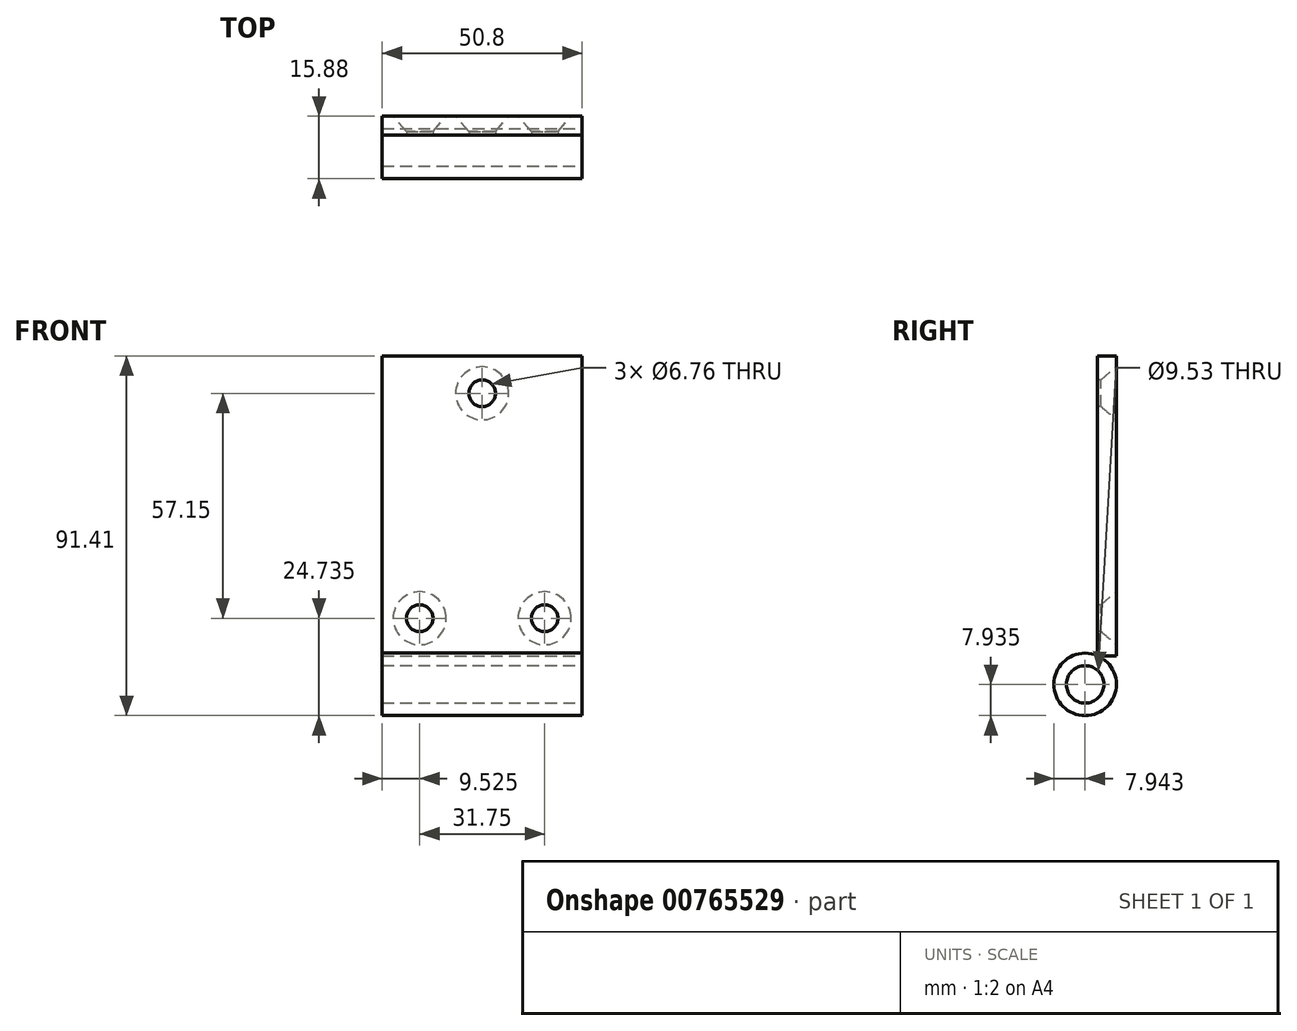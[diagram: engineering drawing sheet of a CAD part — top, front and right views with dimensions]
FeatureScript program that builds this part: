
annotation { "Feature Type Name" : "Feature", "Feature Type Description" : "" }
export const myFeature = defineFeature(function(context is Context, id is Id, definition is map)
    precondition{}
    {
        {
            var Q0;
            Q0=qCreatedBy(makeId("Front.planeOp"),FACE);
            var sketch = newSketch(context, id + "F0", { "sketchPlane" : qUnion([Q0])});
            skLineSegment(sketch, "E0.bottom", {"start": v(-25.4, 38.1) * mm, "end": v(25.4, 38.1) * mm});
            skLineSegment(sketch, "E0.top", {"start": v(-25.4, -38.1) * mm, "end": v(25.4, -38.1) * mm});
            skLineSegment(sketch, "E0.left", {"start": v(-25.4, 38.1) * mm, "end": v(-25.4, -38.1) * mm});
            skLineSegment(sketch, "E0.right", {"start": v(25.4, 38.1) * mm, "end": v(25.4, -38.1) * mm});
            skPoint(sketch, "E0.middle", {"position": v(0, 0) * mm});
            skCircle(sketch, "E1", {"center": v(0, 28.57) * mm, "radius": 3.43 * mm});
            skCircle(sketch, "E2", {"center": v(-15.87, -28.58) * mm, "radius": 3.43 * mm});
            skCircle(sketch, "E3", {"center": v(15.88, -28.58) * mm, "radius": 3.43 * mm});
            skSolve(sketch);
        }
        {
            var Q0;
            Q0=makeQuery(id+"F0.imprint","IMPRINT",FACE,{"disambiguationData":[TD([[makeQuery(id+"F0.imprint","IMPRINT",EDGE,{"derivedFrom":sQuery(id+"F0.wireOp",EDGE,"E0.bottom")}),-1.0]])]});
            var Q1;
            Q1=makeQuery(id+"F0.imprint","IMPRINT",FACE,{"disambiguationData":[TD([[makeQuery(id+"F0.imprint","IMPRINT",EDGE,{"derivedFrom":sQuery(id+"F0.wireOp",EDGE,"E1")}),1.0]])]});
            var Q2;
            Q2=makeQuery(id+"F0.imprint","IMPRINT",FACE,{"disambiguationData":[TD([[makeQuery(id+"F0.imprint","IMPRINT",EDGE,{"derivedFrom":sQuery(id+"F0.wireOp",EDGE,"E2")}),1.0]])]});
            var Q3;
            Q3=makeQuery(id+"F0.imprint","IMPRINT",FACE,{"disambiguationData":[TD([[makeQuery(id+"F0.imprint","IMPRINT",EDGE,{"derivedFrom":sQuery(id+"F0.wireOp",EDGE,"E3")}),1.0]])]});
            extrude(context, id + "F1", {"entities" : qUnion([Q0, Q1, Q2, Q3]), "depth" : 4.76 * mm, "offsetDistance" : 25.4 * mm});
        }
        {
            var Q0;
            Q0=sQuery(id+"F0.wireOp",VERTEX,"E1.center");
            var Q1;
            Q1=sQuery(id+"F0.wireOp",VERTEX,"E2.center");
            var Q2;
            Q2=sQuery(id+"F0.wireOp",VERTEX,"E3.center");
            var Q3;
            Q3=makeQuery(id+"F1.opExtrude","SWEPT_BODY",BODY,{"disambiguationData":[OSD([sQuery(id+"F0.wireOp",EDGE,"E0.bottom"),sQuery(id+"F0.wireOp",EDGE,"E0.top"),sQuery(id+"F0.wireOp",EDGE,"E0.left"),sQuery(id+"F0.wireOp",EDGE,"E0.right")])]});
            hole(context, id + "F2", {"style" : HoleStyle.C_SINK, "endStyle" : HoleEndStyle.THROUGH, "oppositeDirection" : true, "standardTappedOrClearance" : lookupTablePath({ "fit" : "Normal (ASME)", "standard" : "ANSI", "size" : "1/4", "type" : "Clearance" }), "standardBlindInLast" : lookupTablePath({ "fit" : "Free", "standard" : "ANSI", "size" : "1/4", "type" : "Clearance" }), "holeDiameter" : 6.76 * mm, "cSinkDiameter" : 13.5 * mm, "cSinkAngle" : 82 * degree, "majorDiameter" : 6.35 * mm, "isTappedThrough" : true, "tappedDepth" : 6.02 * mm, "tapClearance" : 3, "locations" : qUnion([Q0, Q1, Q2]), "scope" : qUnion([Q3])});
        }
        {
            var Q0;
            Q0=qCreatedBy(makeId("Right.planeOp"),FACE);
            var sketch = newSketch(context, id + "F3", { "sketchPlane" : qUnion([Q0])});
            skCircle(sketch, "E4", {"center": v(-7.94, -45.37) * mm, "radius": 7.94 * mm});
            skCircle(sketch, "E5", {"center": v(-7.94, -45.37) * mm, "radius": 4.76 * mm});
            skSolve(sketch);
        }
        {
            var Q0;
            Q0 = qSketchRegion(id + "F3", true);
            extrude(context, id + "F4", {"entities" : qUnion([Q0]), "oppositeDirection" : true, "depth" : 50.8 * mm, "offsetDistance" : 25.4 * mm, "symmetric" : true});
        }
    });
